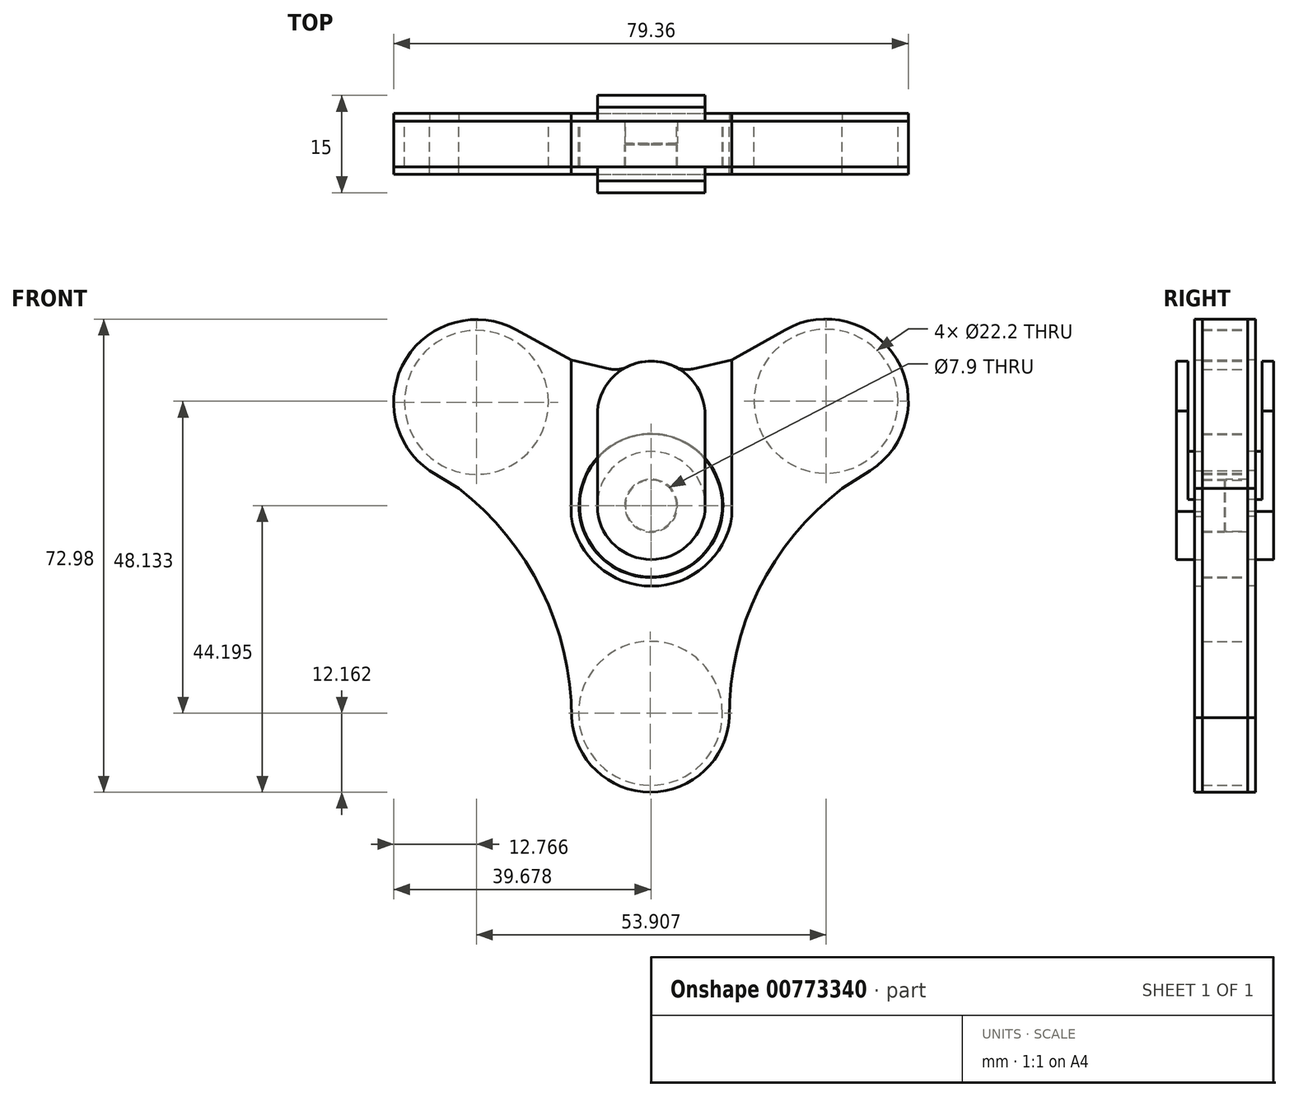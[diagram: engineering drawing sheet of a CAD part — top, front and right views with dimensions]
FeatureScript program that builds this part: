
annotation { "Feature Type Name" : "Feature", "Feature Type Description" : "" }
export const myFeature = defineFeature(function(context is Context, id is Id, definition is map)
    precondition{}
    {
        {
            var Q0;
            Q0=qCreatedBy(makeId("Front.planeOp"),FACE);
            var sketch = newSketch(context, id + "F0", { "sketchPlane" : qUnion([Q0])});
            skLineSegment(sketch, "E0", {"start": v(-10.94, 29.86) * mm, "end": v(-10.94, 10.45) * mm});
            skLineSegment(sketch, "E1", {"start": v(9.76, 29.86) * mm, "end": v(9.76, 10.45) * mm});
            skArc(sketch, "E2", {"start": v(-10.94, 10.45) * mm, "mid": v(-0.59, 1.22) * mm, "end": v(9.76, 10.45) * mm});
            skArc(sketch, "E3", {"start": v(9.76, 29.86) * mm, "mid": v(-0.59, 39.46) * mm, "end": v(-10.94, 29.86) * mm});
            skLineSegment(sketch, "E4", {"start": v(14.96, 39.72) * mm, "end": v(14.96, 9.5) * mm});
            skLineSegment(sketch, "E5", {"start": v(-16, 9.5) * mm, "end": v(-16, 39.72) * mm});
            skArc(sketch, "E6", {"start": v(-16, 9.5) * mm, "mid": v(-0.52, -3.9) * mm, "end": v(14.96, 9.5) * mm});
            skArc(sketch, "E7", {"start": v(-15.9, -29.26) * mm, "mid": v(-21.7, -4.65) * mm, "end": v(-37.7, 14.93) * mm});
            skArc(sketch, "E8", {"start": v(-15.9, -29.26) * mm, "mid": v(-0.72, -43.64) * mm, "end": v(14.46, -29.26) * mm});
            skArc(sketch, "E9", {"start": v(36.27, 14.93) * mm, "mid": v(20.15, -4.6) * mm, "end": v(14.46, -29.26) * mm});
            skLineSegment(sketch, "E10", {"start": v(14.96, 39.72) * mm, "end": v(25.29, 45.52) * mm});
            skLineSegment(sketch, "E11", {"start": v(36.27, 14.93) * mm, "end": v(41.65, 18.35) * mm});
            skLineSegment(sketch, "E12", {"start": v(-43.26, 18.35) * mm, "end": v(-37.7, 14.93) * mm});
            skLineSegment(sketch, "E13", {"start": v(-16, 39.72) * mm, "end": v(-26.58, 45.52) * mm});
            skArc(sketch, "E14", {"start": v(41.65, 18.35) * mm, "mid": v(46.72, 39.91) * mm, "end": v(25.29, 45.52) * mm});
            skArc(sketch, "E15", {"start": v(-26.58, 45.52) * mm, "mid": v(-47.86, 39.87) * mm, "end": v(-43.26, 18.35) * mm});
            skPoint(sketch, "E16.rect.middle", {"position": v(0, 0) * mm});
            skSolve(sketch);
        }
        {
            var Q0;
            Q0=makeQuery(id+"F0.imprint","IMPRINT",FACE,{"disambiguationData":[TD([[makeQuery(id+"F0.imprint","IMPRINT",EDGE,{"derivedFrom":sQuery(id+"F0.wireOp",EDGE,"E4")}),1.0]])]});
            extrude(context, id + "F1", {"entities" : qUnion([Q0]), "depth" : 5.88 * mm, "hasSecondDirection" : true, "secondDirectionOppositeDirection" : false, "secondDirectionDepth" : 4.38 * mm, "offsetDistance" : 25.4 * mm});
        }
        {
            var Q0;
            Q0=qCreatedBy(makeId("Front.planeOp"),FACE);
            var sketch = newSketch(context, id + "F2", { "sketchPlane" : qUnion([Q0])});
            skArc(sketch, "E17", {"start": v(4.04, 38.38) * mm, "mid": v(-0.59, 39.46) * mm, "end": v(-5.2, 38.38) * mm});
            skArc(sketch, "E18", {"start": v(-15.9, -29.26) * mm, "mid": v(-21.7, -4.65) * mm, "end": v(-37.7, 14.93) * mm});
            skArc(sketch, "E19", {"start": v(-15.9, -29.26) * mm, "mid": v(-0.72, -43.64) * mm, "end": v(14.46, -29.26) * mm});
            skArc(sketch, "E20", {"start": v(36.27, 14.93) * mm, "mid": v(20.15, -4.6) * mm, "end": v(14.46, -29.26) * mm});
            skLineSegment(sketch, "E21", {"start": v(14.96, 39.72) * mm, "end": v(25.29, 45.52) * mm});
            skLineSegment(sketch, "E22", {"start": v(36.27, 14.93) * mm, "end": v(41.65, 18.35) * mm});
            skLineSegment(sketch, "E23", {"start": v(-43.26, 18.35) * mm, "end": v(-37.7, 14.93) * mm});
            skLineSegment(sketch, "E24", {"start": v(-16, 39.72) * mm, "end": v(-26.58, 45.52) * mm});
            skArc(sketch, "E25", {"start": v(41.65, 18.35) * mm, "mid": v(46.72, 39.91) * mm, "end": v(25.29, 45.52) * mm});
            skArc(sketch, "E26", {"start": v(-26.58, 45.52) * mm, "mid": v(-47.86, 39.87) * mm, "end": v(-43.26, 18.35) * mm});
            skPoint(sketch, "E27.rect.middle", {"position": v(0, 0) * mm});
            skLineSegment(sketch, "E28", {"start": v(14.96, 39.72) * mm, "end": v(7.38, 37.98) * mm});
            skLineSegment(sketch, "E29", {"start": v(-8.57, 37.99) * mm, "end": v(-16, 39.72) * mm});
            skArc(sketch, "E30.filletArc", {"start": v(4.04, 38.38) * mm, "mid": v(5.67, 37.89) * mm, "end": v(7.38, 37.98) * mm});
            skArc(sketch, "E31.filletArc", {"start": v(-8.57, 37.99) * mm, "mid": v(-6.85, 37.9) * mm, "end": v(-5.2, 38.38) * mm});
            skCircle(sketch, "E32", {"center": v(-0.61, 11.6) * mm, "radius": 13.88 * mm});
            skCircle(sketch, "E33", {"center": v(-34.25, 31.52) * mm, "radius": 13.88 * mm});
            skCircle(sketch, "E34", {"center": v(33.13, 31.73) * mm, "radius": 13.88 * mm});
            skCircle(sketch, "E35", {"center": v(-0.72, -28.44) * mm, "radius": 13.88 * mm});
            skSolve(sketch);
        }
        {
            var Q0;
            Q0=qSketchRegion(id+"F2",true);
            extrude(context, id + "F3", {"entities" : qUnion([Q0]), "depth" : 8.75 * mm, "offsetDistance" : 25 * mm, "symmetric" : true});
        }
        {
            var Q0;
            Q0=qCreatedBy(makeId("Front.planeOp"),FACE);
            var sketch = newSketch(context, id + "F4", { "sketchPlane" : qUnion([Q0])});
            skLineSegment(sketch, "E36", {"start": v(14.96, 39.72) * mm, "end": v(14.96, 9.5) * mm});
            skLineSegment(sketch, "E37", {"start": v(-16, 9.5) * mm, "end": v(-16, 39.72) * mm});
            skArc(sketch, "E38", {"start": v(-16, 9.5) * mm, "mid": v(-0.52, -3.9) * mm, "end": v(14.96, 9.5) * mm});
            skArc(sketch, "E39", {"start": v(-15.9, -29.26) * mm, "mid": v(-21.7, -4.65) * mm, "end": v(-37.7, 14.93) * mm});
            skArc(sketch, "E40", {"start": v(-15.9, -29.26) * mm, "mid": v(-0.72, -43.64) * mm, "end": v(14.46, -29.26) * mm});
            skArc(sketch, "E41", {"start": v(36.27, 14.93) * mm, "mid": v(20.15, -4.6) * mm, "end": v(14.46, -29.26) * mm});
            skLineSegment(sketch, "E42", {"start": v(14.96, 39.72) * mm, "end": v(25.29, 45.52) * mm});
            skLineSegment(sketch, "E43", {"start": v(36.27, 14.93) * mm, "end": v(41.65, 18.35) * mm});
            skLineSegment(sketch, "E44", {"start": v(-43.26, 18.35) * mm, "end": v(-37.7, 14.93) * mm});
            skLineSegment(sketch, "E45", {"start": v(-16, 39.72) * mm, "end": v(-26.58, 45.52) * mm});
            skArc(sketch, "E46", {"start": v(41.65, 18.35) * mm, "mid": v(46.72, 39.91) * mm, "end": v(25.29, 45.52) * mm});
            skArc(sketch, "E47", {"start": v(-26.58, 45.52) * mm, "mid": v(-47.86, 39.87) * mm, "end": v(-43.26, 18.35) * mm});
            skPoint(sketch, "E48.rect.middle", {"position": v(0, 0) * mm});
            skSolve(sketch);
        }
        {
            var Q0;
            Q0=qSketchRegion(id+"F4",true);
            extrude(context, id + "F5", {"entities" : qUnion([Q0]), "oppositeDirection" : true, "depth" : 5.88 * mm, "offsetDistance" : 25 * mm, "hasSecondDirection" : true, "secondDirectionOppositeDirection" : true, "secondDirectionDepth" : 4.38 * mm});
        }
        {
            var Q0;
            Q0=qCreatedBy(makeId("Front.planeOp"),FACE);
            var sketch = newSketch(context, id + "F6", { "sketchPlane" : qUnion([Q0])});
            skLineSegment(sketch, "E49", {"start": v(-10.94, 29.86) * mm, "end": v(-10.94, 10.45) * mm});
            skLineSegment(sketch, "E50", {"start": v(9.76, 29.86) * mm, "end": v(9.76, 10.45) * mm});
            skArc(sketch, "E51", {"start": v(-10.94, 10.45) * mm, "mid": v(-0.59, 1.22) * mm, "end": v(9.76, 10.45) * mm});
            skArc(sketch, "E52", {"start": v(9.76, 29.86) * mm, "mid": v(-0.59, 39.46) * mm, "end": v(-10.94, 29.86) * mm});
            skPoint(sketch, "E53.rect.middle", {"position": v(0, 0) * mm});
            skSolve(sketch);
        }
        {
            var Q0;
            Q0=qCreatedBy(makeId("Front.planeOp"),FACE);
            var sketch = newSketch(context, id + "F7", { "sketchPlane" : qUnion([Q0])});
            skLineSegment(sketch, "E54", {"start": v(-10.94, 29.86) * mm, "end": v(-10.94, 10.45) * mm});
            skLineSegment(sketch, "E55", {"start": v(9.76, 29.86) * mm, "end": v(9.76, 10.45) * mm});
            skArc(sketch, "E56", {"start": v(-10.94, 10.45) * mm, "mid": v(-0.59, 1.22) * mm, "end": v(9.76, 10.45) * mm});
            skArc(sketch, "E57", {"start": v(9.76, 29.86) * mm, "mid": v(-0.59, 39.46) * mm, "end": v(-10.94, 29.86) * mm});
            skPoint(sketch, "E58.rect.middle", {"position": v(0, 0) * mm});
            skSolve(sketch);
        }
        {
            var Q0;
            Q0=qCreatedBy(makeId("Front.planeOp"),FACE);
            var sketch = newSketch(context, id + "F8", { "sketchPlane" : qUnion([Q0])});
            skPoint(sketch, "E59.rect.middle", {"position": v(0, 0) * mm});
            skArc(sketch, "E60", {"start": v(9.76, 12.82) * mm, "mid": v(-0.59, 22.05) * mm, "end": v(-10.94, 12.82) * mm});
            skLineSegment(sketch, "E61", {"start": v(-10.94, 12.82) * mm, "end": v(-10.94, 10.45) * mm});
            skLineSegment(sketch, "E62", {"start": v(9.76, 12.82) * mm, "end": v(9.76, 10.45) * mm});
            skArc(sketch, "E63", {"start": v(-10.94, 10.45) * mm, "mid": v(-0.59, 1.22) * mm, "end": v(9.76, 10.45) * mm});
            skArc(sketch, "E64", {"start": v(9.76, 29.86) * mm, "mid": v(-0.59, 39.46) * mm, "end": v(-10.94, 29.86) * mm});
            skSolve(sketch);
        }
        {
            var Q0;
            Q0=qCreatedBy(makeId("Front.planeOp"),FACE);
            var sketch = newSketch(context, id + "F9", { "sketchPlane" : qUnion([Q0])});
            skPoint(sketch, "E65.rect.middle", {"position": v(0, 0) * mm});
            skArc(sketch, "E66", {"start": v(9.76, 12.82) * mm, "mid": v(-0.59, 22.05) * mm, "end": v(-10.94, 12.82) * mm});
            skLineSegment(sketch, "E67", {"start": v(-10.94, 12.82) * mm, "end": v(-10.94, 10.45) * mm});
            skLineSegment(sketch, "E68", {"start": v(9.76, 12.82) * mm, "end": v(9.76, 10.45) * mm});
            skArc(sketch, "E69", {"start": v(-10.94, 10.45) * mm, "mid": v(-0.59, 1.22) * mm, "end": v(9.76, 10.45) * mm});
            skArc(sketch, "E70", {"start": v(9.76, 29.86) * mm, "mid": v(-0.59, 39.46) * mm, "end": v(-10.94, 29.86) * mm});
            skSolve(sketch);
        }
        {
            var Q0;
            Q0=qSketchRegion(id+"F6",true);
            extrude(context, id + "F10", {"entities" : qUnion([Q0]), "depth" : 9.38 * mm, "offsetDistance" : 25 * mm, "hasSecondDirection" : true, "secondDirectionOppositeDirection" : false, "secondDirectionDepth" : 7.12 * mm});
        }
        {
            var Q0;
            Q0=qSketchRegion(id+"F7",true);
            extrude(context, id + "F11", {"entities" : qUnion([Q0]), "oppositeDirection" : true, "depth" : 7.5 * mm, "offsetDistance" : 25 * mm, "hasSecondDirection" : true, "secondDirectionOppositeDirection" : true, "secondDirectionDepth" : 5.5 * mm});
        }
        {
            var Q0;
            Q0=qSketchRegion(id+"F8",true);
            var Q1;
            Q1=makeQuery(id+"F8.imprint","IMPRINT",FACE,{"disambiguationData":[TD([[makeQuery(id+"F8.imprint","IMPRINT",EDGE,{"derivedFrom":sQuery(id+"F8.wireOp",EDGE,"nhQDkZJl-LwPV-CaPN-FJ2m-8GQ3NmPbg96J")}),1.0]])]});
            extrude(context, id + "F12", {"entities" : qUnion([Q0, Q1]), "operationType" : NewBodyOperationType.ADD, "depth" : 7.12 * mm, "offsetDistance" : 25 * mm, "hasSecondDirection" : true, "secondDirectionOppositeDirection" : false, "secondDirectionDepth" : 4.38 * mm});
        }
        {
            var Q0;
            Q0=qSketchRegion(id+"F9",true);
            extrude(context, id + "F13", {"entities" : qUnion([Q0]), "operationType" : NewBodyOperationType.ADD, "oppositeDirection" : true, "depth" : 5.5 * mm, "offsetDistance" : 25 * mm, "hasSecondDirection" : true, "secondDirectionOppositeDirection" : true, "secondDirectionDepth" : 3.5 * mm});
        }
        {
            var Q0;
            Q0=qCreatedBy(makeId("Front.planeOp"),FACE);
            var sketch = newSketch(context, id + "F14", { "sketchPlane" : qUnion([Q0])});
            skPoint(sketch, "E71.rect.middle", {"position": v(0, 0) * mm});
            skCircle(sketch, "E72", {"center": v(-0.59, 11.6) * mm, "radius": 5.1 * mm});
            skSolve(sketch);
        }
        {
            var Q0;
            Q0=qCreatedBy(makeId("Front.planeOp"),FACE);
            var sketch = newSketch(context, id + "F15", { "sketchPlane" : qUnion([Q0])});
            skPoint(sketch, "E73.rect.middle", {"position": v(0, 0) * mm});
            skCircle(sketch, "E74", {"center": v(-0.59, 11.64) * mm, "radius": 4.14 * mm});
            skSolve(sketch);
        }
        {
            var Q0;
            Q0=qSketchRegion(id+"F14",true);
            extrude(context, id + "F16", {"entities" : qUnion([Q0]), "operationType" : NewBodyOperationType.ADD, "depth" : 4.38 * mm, "offsetDistance" : .395 * mm, "hasSecondDirection" : true, "secondDirectionOppositeDirection" : false, "secondDirectionDepth" : 0.1 * mm});
        }
        {
            var Q0;
            Q0=qSketchRegion(id+"F15",true);
            extrude(context, id + "F17", {"entities" : qUnion([Q0]), "operationType" : NewBodyOperationType.ADD, "oppositeDirection" : true, "depth" : 3.5 * mm, "offsetDistance" : 25 * mm, "hasSecondDirection" : true, "secondDirectionOppositeDirection" : true, "secondDirectionDepth" : .395 * mm});
        }
        {
            var Q0;
            Q0=qCreatedBy(makeId("Front.planeOp"),FACE);
            var sketch = newSketch(context, id + "F18", { "sketchPlane" : qUnion([Q0])});
            skPoint(sketch, "E75.rect.middle", {"position": v(0, 0) * mm});
            skCircle(sketch, "E76", {"center": v(-0.61, 11.6) * mm, "radius": 13.75 * mm});
            skCircle(sketch, "E77", {"center": v(-0.61, 11.6) * mm, "radius": 4.94 * mm});
            skSolve(sketch);
        }
        {
            var Q0;
            Q0=qSketchRegion(id+"F18",true);
            extrude(context, id + "F19", {"entities" : qUnion([Q0]), "depth" : 8.75 * mm, "offsetDistance" : 25 * mm, "symmetric" : true});
        }
        {
            var Q0;
            Q0=makeQuery(id+"F3.opExtrude","SWEPT_BODY",BODY,{"disambiguationData":[OSD([sQuery(id+"F2.wireOp",EDGE,"E17"),sQuery(id+"F2.wireOp",EDGE,"E18"),sQuery(id+"F2.wireOp",EDGE,"E19"),sQuery(id+"F2.wireOp",EDGE,"E20"),sQuery(id+"F2.wireOp",EDGE,"E21"),sQuery(id+"F2.wireOp",EDGE,"E22"),sQuery(id+"F2.wireOp",EDGE,"E23"),sQuery(id+"F2.wireOp",EDGE,"E24"),sQuery(id+"F2.wireOp",EDGE,"E25"),sQuery(id+"F2.wireOp",EDGE,"E26"),sQuery(id+"F2.wireOp",EDGE,"E28"),sQuery(id+"F2.wireOp",EDGE,"E29"),sQuery(id+"F2.wireOp",EDGE,"E30.filletArc"),sQuery(id+"F2.wireOp",EDGE,"E31.filletArc"),sQuery(id+"F2.wireOp",EDGE,"E32"),sQuery(id+"F2.wireOp",EDGE,"E33"),sQuery(id+"F2.wireOp",EDGE,"E34"),sQuery(id+"F2.wireOp",EDGE,"E35")])]});
            var Q1;
            Q1=makeQuery(id+"F5.opExtrude","SWEPT_BODY",BODY,{"disambiguationData":[OSD([sQuery(id+"F4.wireOp",EDGE,"E36"),sQuery(id+"F4.wireOp",EDGE,"E37"),sQuery(id+"F4.wireOp",EDGE,"E38"),sQuery(id+"F4.wireOp",EDGE,"E39"),sQuery(id+"F4.wireOp",EDGE,"E40"),sQuery(id+"F4.wireOp",EDGE,"E41"),sQuery(id+"F4.wireOp",EDGE,"E42"),sQuery(id+"F4.wireOp",EDGE,"E43"),sQuery(id+"F4.wireOp",EDGE,"E44"),sQuery(id+"F4.wireOp",EDGE,"E45"),sQuery(id+"F4.wireOp",EDGE,"E46"),sQuery(id+"F4.wireOp",EDGE,"E47")])]});
            var Q2;
            Q2=makeQuery(id+"F10.opExtrude","SWEPT_BODY",BODY,{"disambiguationData":[OSD([sQuery(id+"F6.wireOp",EDGE,"E49"),sQuery(id+"F6.wireOp",EDGE,"E50"),sQuery(id+"F6.wireOp",EDGE,"E51"),sQuery(id+"F6.wireOp",EDGE,"E52")])]});
            var Q3;
            Q3=makeQuery(id+"F11.opExtrude","SWEPT_BODY",BODY,{"disambiguationData":[OSD([sQuery(id+"F7.wireOp",EDGE,"E54"),sQuery(id+"F7.wireOp",EDGE,"E55"),sQuery(id+"F7.wireOp",EDGE,"E56"),sQuery(id+"F7.wireOp",EDGE,"E57")])]});
            var Q4;
            Q4=makeQuery(id+"F1.opExtrude","SWEPT_BODY",BODY,{"disambiguationData":[OSD([sQuery(id+"F0.wireOp",EDGE,"E4"),sQuery(id+"F0.wireOp",EDGE,"E5"),sQuery(id+"F0.wireOp",EDGE,"E6"),sQuery(id+"F0.wireOp",EDGE,"E7"),sQuery(id+"F0.wireOp",EDGE,"E8"),sQuery(id+"F0.wireOp",EDGE,"E9"),sQuery(id+"F0.wireOp",EDGE,"E10"),sQuery(id+"F0.wireOp",EDGE,"E11"),sQuery(id+"F0.wireOp",EDGE,"E12"),sQuery(id+"F0.wireOp",EDGE,"E13"),sQuery(id+"F0.wireOp",EDGE,"E14"),sQuery(id+"F0.wireOp",EDGE,"E15")])]});
            var Q5;
            Q5=makeQuery(id+"F19.opExtrude","SWEPT_BODY",BODY,{"disambiguationData":[OSD([sQuery(id+"F18.wireOp",EDGE,"E76"),sQuery(id+"F18.wireOp",EDGE,"E77")])]});
            var Q6;
            Q6=qCreatedBy(makeId("Origin.pointOp"),VERTEX);
            transform(context, id + "F20", {"entities" : qUnion([Q0, Q1, Q2, Q3, Q4, Q5]), "transformType" : TransformType.SCALE_UNIFORMLY, "scale" : .8, "scalePoint" : qUnion([Q6]), "makeCopy" : false});
        }
        {
            var Q0;
            Q0=makeQuery(id+"F11.opExtrude","SWEPT_BODY",BODY,{"disambiguationData":[OSD([sQuery(id+"F7.wireOp",EDGE,"E54"),sQuery(id+"F7.wireOp",EDGE,"E55"),sQuery(id+"F7.wireOp",EDGE,"E56"),sQuery(id+"F7.wireOp",EDGE,"E57")])]});
            deleteBodies(context, id + "F21", {"entities" : qUnion([Q0])});
        }
        {
            var Q0;
            Q0=makeQuery(id+"F10.opExtrude","SWEPT_BODY",BODY,{"disambiguationData":[OSD([sQuery(id+"F6.wireOp",EDGE,"E49"),sQuery(id+"F6.wireOp",EDGE,"E50"),sQuery(id+"F6.wireOp",EDGE,"E51"),sQuery(id+"F6.wireOp",EDGE,"E52")])]});
            var Q1;
            Q1=qCreatedBy(makeId("Front.planeOp"),FACE);
            mirror(context, id + "F22", {"entities" : qUnion([Q0]), "mirrorPlane" : qUnion([Q1])});
        }
    });
